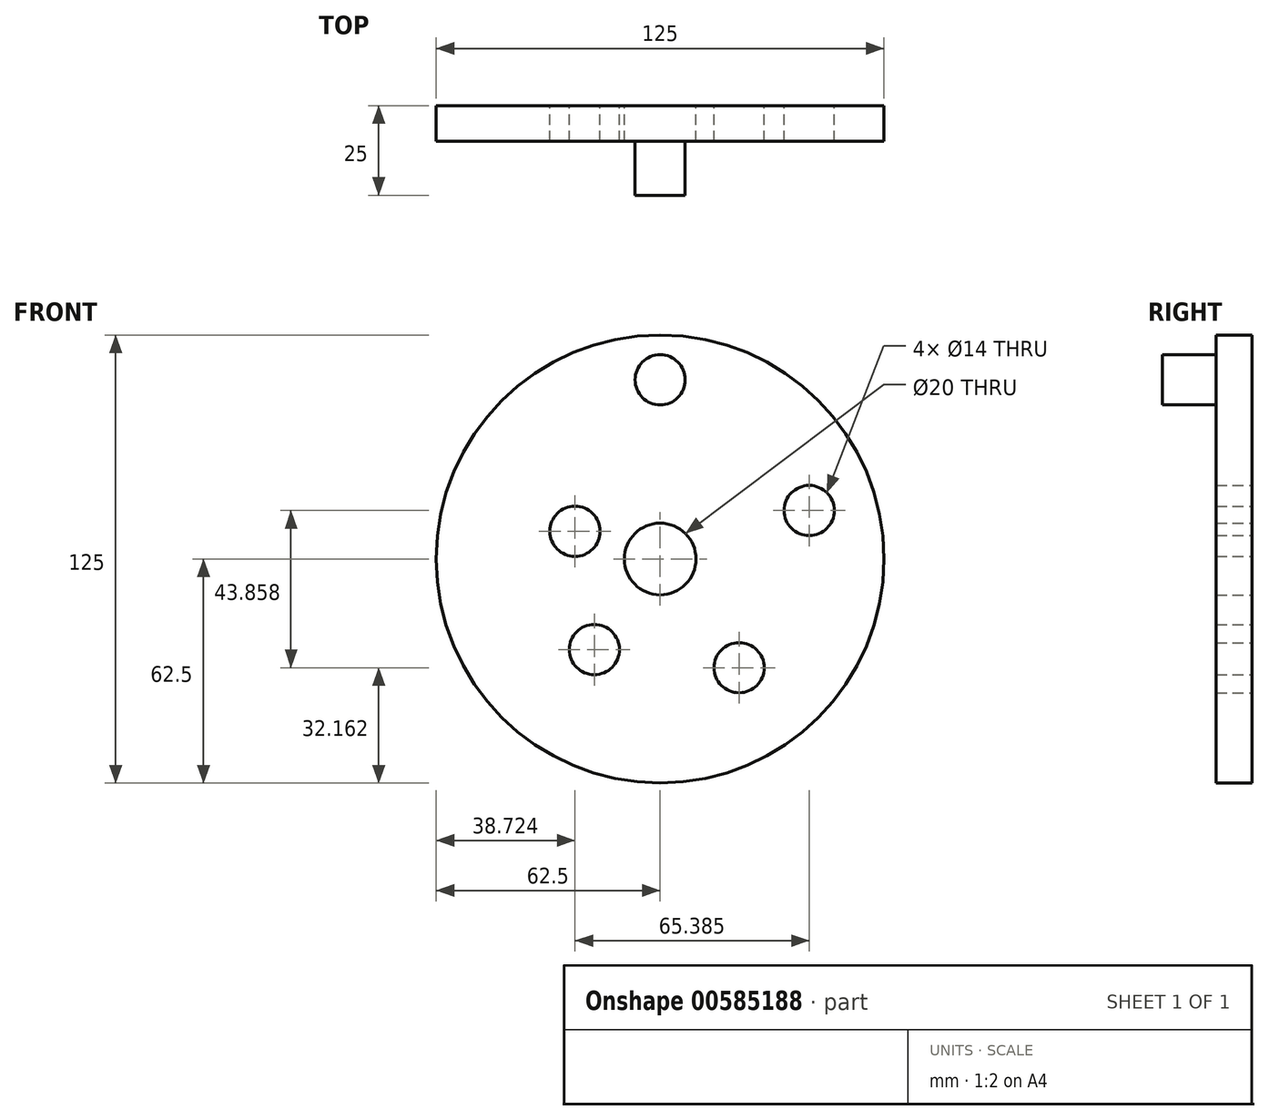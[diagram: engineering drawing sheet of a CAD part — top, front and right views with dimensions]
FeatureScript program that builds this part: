
annotation { "Feature Type Name" : "Feature", "Feature Type Description" : "" }
export const myFeature = defineFeature(function(context is Context, id is Id, definition is map)
    precondition{}
    {
        {
            var Q0;
            Q0=qCreatedBy(makeId("Front.planeOp"),FACE);
            var sketch = newSketch(context, id + "F0", { "sketchPlane" : qUnion([Q0])});
            skCircle(sketch, "E0", {"center": v(0, 0) * mm, "radius": 50 * mm, "construction": true});
            skCircle(sketch, "E1", {"center": v(0, 0) * mm, "radius": 25 * mm, "construction": true});
            skCircle(sketch, "E2", {"center": v(0, 0) * mm, "radius": 31.25 * mm, "construction": true});
            skCircle(sketch, "E3", {"center": v(0, 0) * mm, "radius": 43.75 * mm, "construction": true});
            skCircle(sketch, "E4", {"center": v(0, 0) * mm, "radius": 37.5 * mm, "construction": true});
            skCircle(sketch, "E5", {"center": v(0, 0) * mm, "radius": 62.5 * mm});
            skLineSegment(sketch, "E6", {"start": v(0, 0) * mm, "end": v(0, 50) * mm, "construction": true});
            skCircle(sketch, "E7", {"center": v(0, 50) * mm, "radius": 7 * mm});
            skCircle(sketch, "E8", {"center": v(41.6, 13.52) * mm, "radius": 7 * mm});
            skCircle(sketch, "E9", {"center": v(22.04, -30.34) * mm, "radius": 7 * mm});
            skCircle(sketch, "E10", {"center": v(-18.37, -25.28) * mm, "radius": 7 * mm});
            skCircle(sketch, "E11", {"center": v(-23.78, 7.73) * mm, "radius": 7 * mm});
            skLineSegment(sketch, "E12", {"start": v(41.6, 13.52) * mm, "end": v(0, 0) * mm, "construction": true});
            skLineSegment(sketch, "E13", {"start": v(22.04, -30.34) * mm, "end": v(0, 0) * mm, "construction": true});
            skLineSegment(sketch, "E14", {"start": v(-18.37, -25.28) * mm, "end": v(0, 0) * mm, "construction": true});
            skLineSegment(sketch, "E15", {"start": v(0, 0) * mm, "end": v(-23.78, 7.73) * mm, "construction": true});
            skCircle(sketch, "E16", {"center": v(0, 0) * mm, "radius": 10 * mm});
            skSolve(sketch);
        }
        {
            var Q0;
            Q0 = qSketchRegion(id + "F0", true);
            extrude(context, id + "F1", {"entities" : qUnion([Q0]), "depth" : 10 * mm, "offsetDistance" : 25 * mm});
        }
        {
            var Q0;
            Q0=qCreatedBy(makeId("Front.planeOp"),FACE);
            var sketch = newSketch(context, id + "F2", { "sketchPlane" : qUnion([Q0])});
            skCircle(sketch, "E17", {"center": v(0, 50) * mm, "radius": 7 * mm});
            skSolve(sketch);
        }
        {
            var Q0;
            Q0 = qSketchRegion(id + "F2", true);
            extrude(context, id + "F3", {"entities" : qUnion([Q0]), "operationType" : NewBodyOperationType.ADD, "depth" : 25 * mm, "offsetDistance" : 25 * mm});
        }
    });
